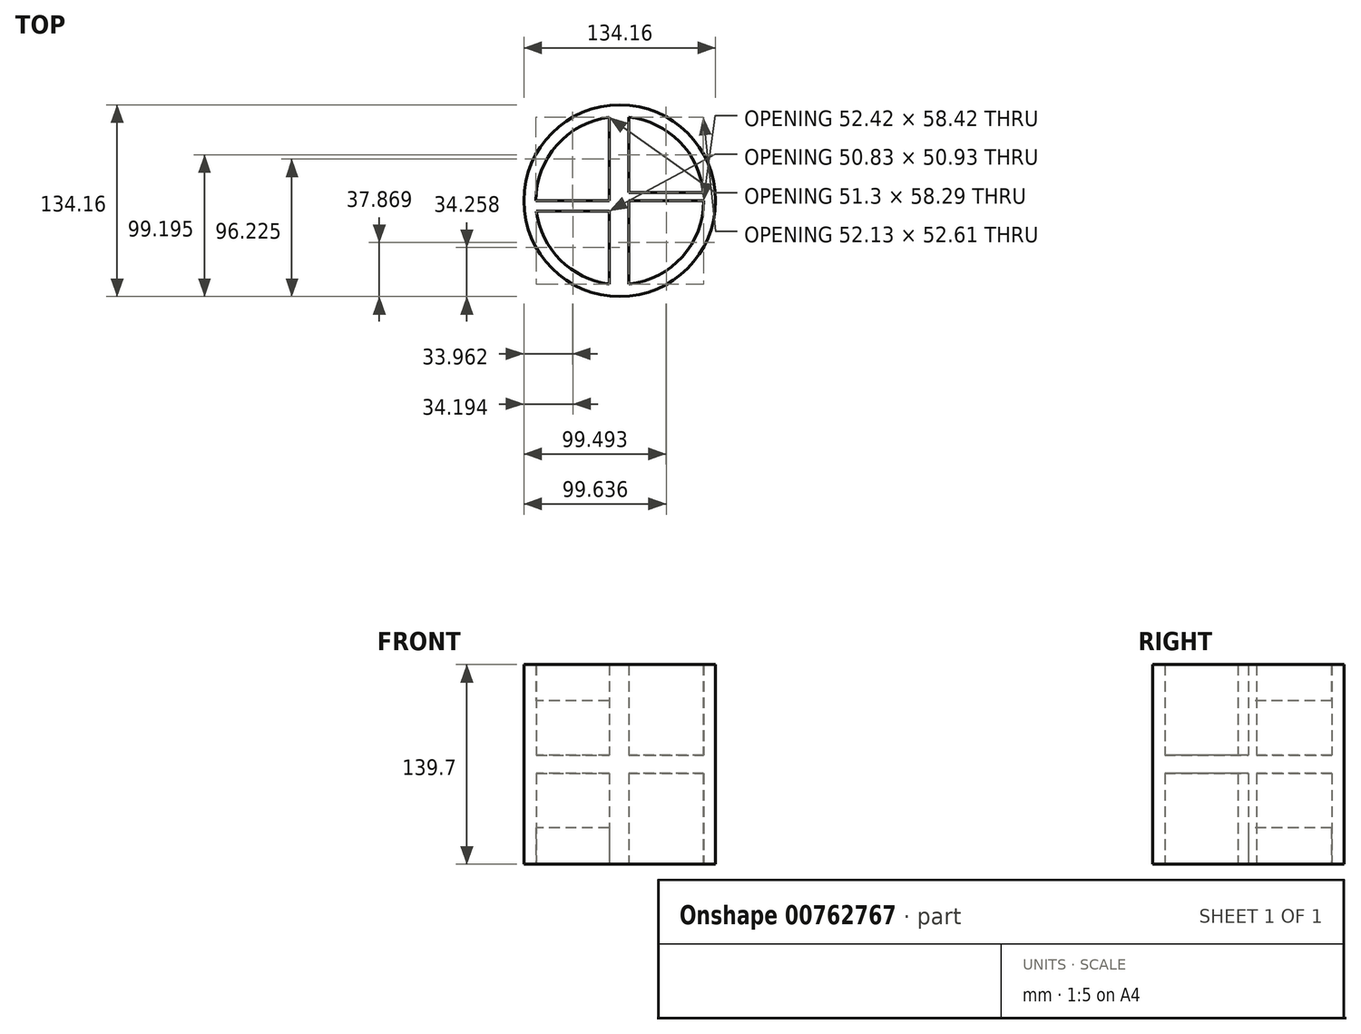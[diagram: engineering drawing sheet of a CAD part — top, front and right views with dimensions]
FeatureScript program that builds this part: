
annotation { "Feature Type Name" : "Feature", "Feature Type Description" : "" }
export const myFeature = defineFeature(function(context is Context, id is Id, definition is map)
    precondition{}
    {
        {
            var Q0;
            Q0=qCreatedBy(makeId("Top.planeOp"),FACE);
            var sketch = newSketch(context, id + "F0", { "sketchPlane" : qUnion([Q0])});
            skCircle(sketch, "E0", {"center": v(0, 0) * mm, "radius": 58.77 * mm});
            skLineSegment(sketch, "E1", {"start": v(-7.47, 58.29) * mm, "end": v(-7.47, -58.29) * mm});
            skLineSegment(sketch, "E2", {"start": v(-7.47, 0) * mm, "end": v(-58.77, 0) * mm});
            skLineSegment(sketch, "E3", {"start": v(6.35, 58.42) * mm, "end": v(6.35, -58.42) * mm});
            skLineSegment(sketch, "E4", {"start": v(6.35, 0) * mm, "end": v(58.77, 0) * mm});
            skLineSegment(sketch, "E5", {"start": v(6.35, 5.8) * mm, "end": v(58.48, 5.8) * mm});
            skLineSegment(sketch, "E6", {"start": v(-7.47, -7.36) * mm, "end": v(-58.3, -7.36) * mm});
            skCircle(sketch, "E7", {"center": v(0, 0) * mm, "radius": 67.08 * mm});
            skSolve(sketch);
        }
        {
            var Q0;
            Q0 = qSketchRegion(id + "F0", true);
            var Q1;
            {var subQ0=sQuery(id+"F0.wireOp",EDGE,"E1");var subQ3=sQuery(id+"F0.wireOp",EDGE,"E0");var subQ4=makeQuery(id+"F0.imprint","INTERSECT",VERTEX,{"disambiguationData":[OD(0.0)],"derivedFrom":[subQ3,subQ0]});Q1=makeQuery(id+"F0.imprint","IMPRINT",FACE,{"disambiguationData":[TD([[makeQuery(id+"F0.imprint","IMPRINT",EDGE,{"disambiguationData":[TD([[subQ4,1.0]])],"derivedFrom":subQ3}),1.0]])]});}
            var Q2;
            {var subQ0=sQuery(id+"F0.wireOp",EDGE,"E4");Q2=makeQuery(id+"F0.imprint","IMPRINT",FACE,{"disambiguationData":[TD([[makeQuery(id+"F0.imprint","IMPRINT",EDGE,{"derivedFrom":subQ0}),1.0]])]});}
            var Q3;
            {var subQ0=sQuery(id+"F0.wireOp",EDGE,"E2");Q3=makeQuery(id+"F0.imprint","IMPRINT",FACE,{"disambiguationData":[TD([[makeQuery(id+"F0.imprint","IMPRINT",EDGE,{"derivedFrom":subQ0}),1.0]])]});}
            extrude(context, id + "F1", {"entities" : qUnion([Q0, Q1, Q2, Q3]), "endBound" : BoundingType.SYMMETRIC, "depth" : 139.7 * mm, "offsetDistance" : 25.4 * mm});
        }
        {
            var Q0;
            {var subQ3=sQuery(id+"F0.wireOp",EDGE,"E2");Q0=makeQuery(id+"F0.imprint","IMPRINT",FACE,{"disambiguationData":[TD([[makeQuery(id+"F0.imprint","IMPRINT",EDGE,{"derivedFrom":subQ3}),1.0]])]});}
            var Q1;
            {var subQ3=sQuery(id+"F0.wireOp",EDGE,"2tvhzXV0-d3Ut-THUC-ePR0-RIDJqSIbRzCV");Q1=makeQuery(id+"F0.imprint","IMPRINT",FACE,{"disambiguationData":[TD([[makeQuery(id+"F0.imprint","IMPRINT",EDGE,{"derivedFrom":subQ3}),-1.0]])]});}
            var Q2;
            {var subQ3=sQuery(id+"F0.wireOp",EDGE,"E5");Q2=makeQuery(id+"F0.imprint","IMPRINT",FACE,{"disambiguationData":[TD([[makeQuery(id+"F0.imprint","IMPRINT",EDGE,{"derivedFrom":subQ3}),1.0]])]});}
            var Q3;
            {var subQ3=sQuery(id+"F0.wireOp",EDGE,"E4");Q3=makeQuery(id+"F0.imprint","IMPRINT",FACE,{"disambiguationData":[TD([[makeQuery(id+"F0.imprint","IMPRINT",EDGE,{"derivedFrom":subQ3}),-1.0]])]});}
            var Q4;
            {var subQ3=sQuery(id+"F0.wireOp",EDGE,"E6");Q4=makeQuery(id+"F0.imprint","IMPRINT",FACE,{"disambiguationData":[TD([[makeQuery(id+"F0.imprint","IMPRINT",EDGE,{"derivedFrom":subQ3}),1.0]])]});}
            extrude(context, id + "F2", {"entities" : qUnion([Q0, Q1, Q2, Q3, Q4]), "operationType" : NewBodyOperationType.ADD, "endBound" : BoundingType.SYMMETRIC, "depth" : 12.7 * mm, "offsetDistance" : 25.4 * mm});
        }
        {
            var Q0;
            {var subQ3=sQuery(id+"F0.wireOp",EDGE,"E2");Q0=makeQuery(id+"F0.imprint","IMPRINT",FACE,{"disambiguationData":[TD([[makeQuery(id+"F0.imprint","IMPRINT",EDGE,{"derivedFrom":subQ3}),-1.0]])]});}
            extrude(context, id + "F3", {"entities" : qUnion([Q0]), "operationType" : NewBodyOperationType.ADD, "endBound" : BoundingType.SYMMETRIC, "depth" : 88.9 * mm, "offsetDistance" : 25.4 * mm});
        }
    });
